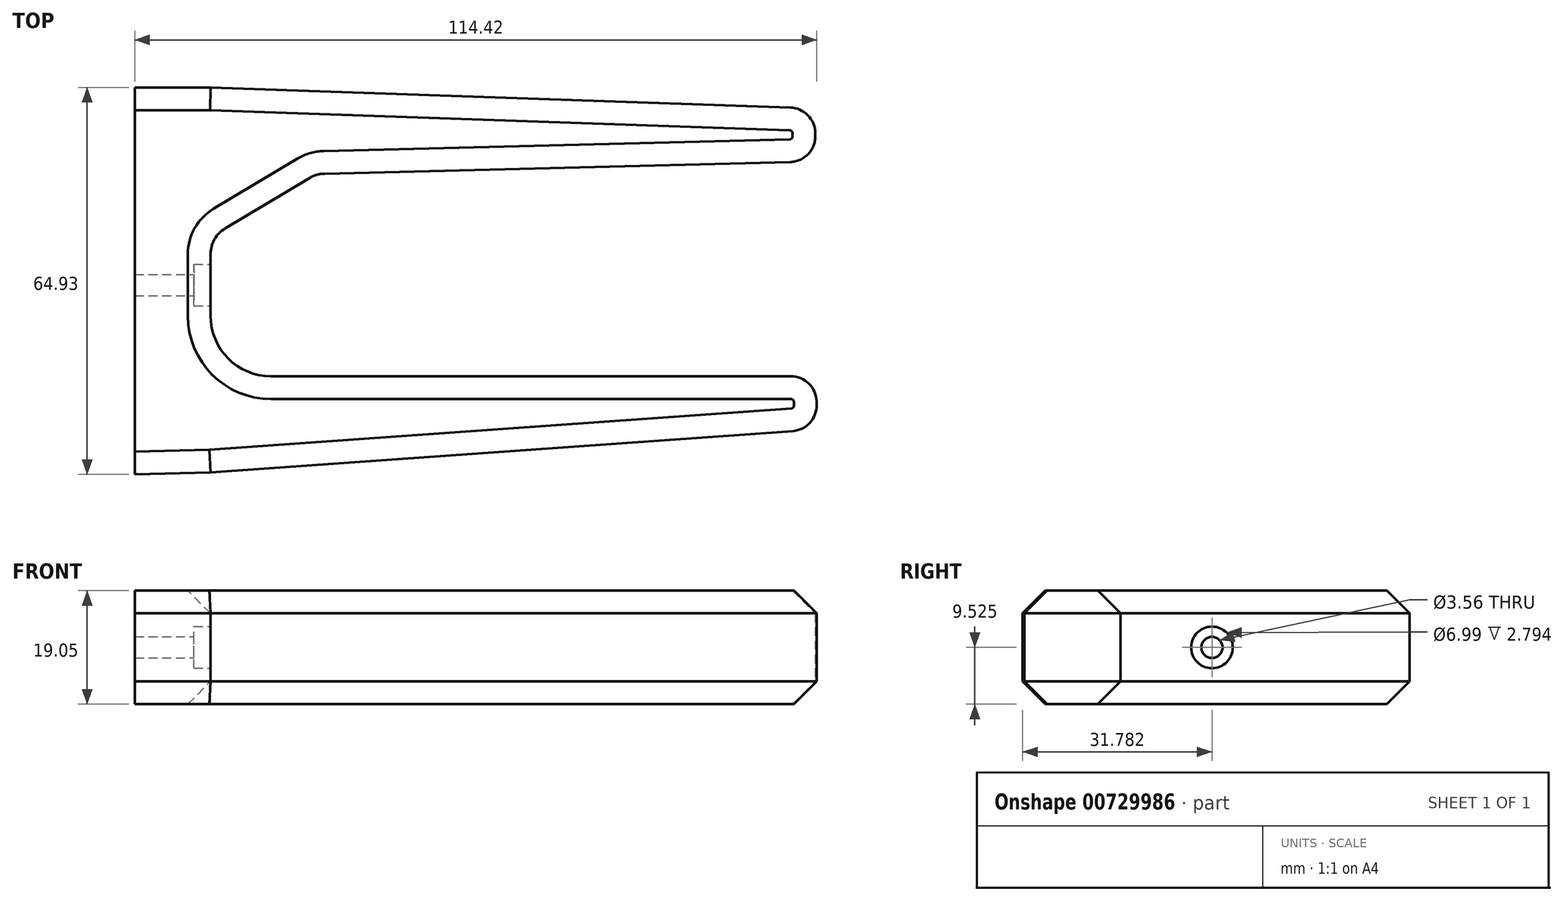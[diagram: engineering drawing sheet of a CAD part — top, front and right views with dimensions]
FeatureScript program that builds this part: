
annotation { "Feature Type Name" : "Feature", "Feature Type Description" : "" }
export const myFeature = defineFeature(function(context is Context, id is Id, definition is map)
    precondition{}
    {
        {
            var Q0;
            Q0=qCreatedBy(makeId("Top.planeOp"),FACE);
            var sketch = newSketch(context, id + "F0", { "sketchPlane" : qUnion([Q0])});
            skLineSegment(sketch, "E0", {"start": v(0, 0) * mm, "end": v(101.6, 0) * mm});
            skLineSegment(sketch, "E1", {"start": v(0, 0) * mm, "end": v(0, 33.53) * mm});
            skLineSegment(sketch, "E2", {"start": v(101.6, 0) * mm, "end": v(101.6, 36.07) * mm});
            skLineSegment(sketch, "E3", {"start": v(0, 33.53) * mm, "end": v(101.6, 36.07) * mm});
            skLineSegment(sketch, "E4", {"start": v(101.6, 36.07) * mm, "end": v(101.38, 44.96) * mm});
            skLineSegment(sketch, "E5", {"start": v(101.38, 44.96) * mm, "end": v(0, 48.47) * mm});
            skLineSegment(sketch, "E6", {"start": v(0, 48.47) * mm, "end": v(-12.7, 48.47) * mm});
            skLineSegment(sketch, "E7", {"start": v(-12.7, 48.47) * mm, "end": v(-12.7, 0) * mm});
            skLineSegment(sketch, "E8", {"start": v(101.6, 0) * mm, "end": v(101.82, -8.89) * mm});
            skLineSegment(sketch, "E9", {"start": v(101.82, -8.89) * mm, "end": v(0, -16.15) * mm});
            skLineSegment(sketch, "E10", {"start": v(0, -16.15) * mm, "end": v(-12.7, -16.46) * mm});
            skLineSegment(sketch, "E11", {"start": v(-12.7, -16.46) * mm, "end": v(-12.7, 0) * mm});
            skSolve(sketch);
        }
        {
            var Q0;
            Q0=makeQuery(id+"F0.imprint","IMPRINT",FACE,{"disambiguationData":[TD([[makeQuery(id+"F0.imprint","IMPRINT",EDGE,{"derivedFrom":sQuery(id+"F0.wireOp",EDGE,"E0")}),-1.0]])]});
            extrude(context, id + "F1", {"entities" : qUnion([Q0]), "depth" : 19.05 * mm, "offsetDistance" : 25.4 * mm});
        }
        {
            var Q0;
            Q0=makeQuery(id+"F1.opExtrude","SWEPT_EDGE",EDGE,{"disambiguationData":[OSD([sQuery(id+"F0.wireOp",EDGE,"E1"),sQuery(id+"F0.wireOp",EDGE,"E3")])]});
            chamfer(context, id + "F2", {"entities" : qUnion([Q0]), "chamferType" : ChamferType.TWO_OFFSETS, "width1" : 10.16 * mm, "oppositeDirection" : true, "width2" : 17.78 * mm, "tangentPropagation" : true});
        }
        {
            var Q0;
            {var subQ0=sQuery(id+"F0.wireOp",EDGE,"E3");Q0=makeQuery(id+"F2.opChamfer","BLEND_EDGE",EDGE,{"blendedFrom":[makeQuery(id+"F1.opExtrude","SWEPT_EDGE",EDGE,{"disambiguationData":[OSD([sQuery(id+"F0.wireOp",EDGE,"E1"),subQ0])]}),makeQuery(id+"F1.opExtrude","SWEPT_FACE",FACE,{"disambiguationData":[OSD([subQ0])]})],"blendedInto":[makeQuery(id+"F1.opExtrude","SWEPT_FACE",FACE,{"disambiguationData":[OSD([subQ0])]})]});}
            var Q1;
            {var subQ0=sQuery(id+"F0.wireOp",EDGE,"E1");Q1=makeQuery(id+"F2.opChamfer","BLEND_EDGE",EDGE,{"blendedFrom":[makeQuery(id+"F1.opExtrude","SWEPT_EDGE",EDGE,{"disambiguationData":[OSD([subQ0,sQuery(id+"F0.wireOp",EDGE,"E3")])]}),makeQuery(id+"F1.opExtrude","SWEPT_FACE",FACE,{"disambiguationData":[OSD([subQ0])]})],"blendedInto":[makeQuery(id+"F1.opExtrude","SWEPT_FACE",FACE,{"disambiguationData":[OSD([subQ0])]})]});}
            fillet(context, id + "F3", {"entities" : qUnion([Q0, Q1]), "radius" : 5.08 * mm, "tangentPropagation" : true, "allowEdgeOverflow" : false});
        }
        {
            var Q0;
            Q0=makeQuery(id+"F1.opExtrude","SWEPT_EDGE",EDGE,{"disambiguationData":[OSD([sQuery(id+"F0.wireOp",EDGE,"E0"),sQuery(id+"F0.wireOp",EDGE,"E1")])]});
            fillet(context, id + "F4", {"entities" : qUnion([Q0]), "radius" : 10.16 * mm, "tangentPropagation" : true, "allowEdgeOverflow" : false});
        }
        {
            var Q0;
            Q0=makeQuery(id+"F1.opExtrude","SWEPT_EDGE",EDGE,{"disambiguationData":[OSD([sQuery(id+"F0.wireOp",EDGE,"E2"),sQuery(id+"F0.wireOp",EDGE,"E3"),sQuery(id+"F0.wireOp",EDGE,"E4")])]});
            var Q1;
            Q1=makeQuery(id+"F1.opExtrude","SWEPT_EDGE",EDGE,{"disambiguationData":[OSD([sQuery(id+"F0.wireOp",EDGE,"E4"),sQuery(id+"F0.wireOp",EDGE,"E5")])]});
            var Q2;
            Q2=makeQuery(id+"F1.opExtrude","SWEPT_EDGE",EDGE,{"disambiguationData":[OSD([sQuery(id+"F0.wireOp",EDGE,"E0"),sQuery(id+"F0.wireOp",EDGE,"E2"),sQuery(id+"F0.wireOp",EDGE,"E8")])]});
            var Q3;
            Q3=makeQuery(id+"F1.opExtrude","SWEPT_EDGE",EDGE,{"disambiguationData":[OSD([sQuery(id+"F0.wireOp",EDGE,"E8"),sQuery(id+"F0.wireOp",EDGE,"E9")])]});
            fillet(context, id + "F5", {"entities" : qUnion([Q0, Q1, Q2, Q3]), "radius" : 4.32 * mm, "tangentPropagation" : true, "allowEdgeOverflow" : false});
        }
        {
            var Q0;
            Q0=makeQuery(id+"F1.opExtrude","CAP_EDGE",EDGE,{"disambiguationData":[OSD([sQuery(id+"F0.wireOp",EDGE,"E6")])],"isStart":false});
            var Q1;
            Q1=makeQuery(id+"F1.opExtrude","CAP_EDGE",EDGE,{"disambiguationData":[OSD([sQuery(id+"F0.wireOp",EDGE,"E10")])],"isStart":false});
            var Q2;
            Q2=makeQuery(id+"F1.opExtrude","CAP_EDGE",EDGE,{"disambiguationData":[OSD([sQuery(id+"F0.wireOp",EDGE,"E6")])],"isStart":true});
            var Q3;
            Q3=makeQuery(id+"F1.opExtrude","CAP_EDGE",EDGE,{"disambiguationData":[OSD([sQuery(id+"F0.wireOp",EDGE,"E10")])],"isStart":true});
            var Q4;
            Q4=makeQuery(id+"F1.opExtrude","CAP_EDGE",EDGE,{"disambiguationData":[OSD([sQuery(id+"F0.wireOp",EDGE,"E3")])],"isStart":false});
            var Q5;
            Q5=makeQuery(id+"F1.opExtrude","CAP_EDGE",EDGE,{"disambiguationData":[OSD([sQuery(id+"F0.wireOp",EDGE,"E3")])],"isStart":true});
            chamfer(context, id + "F6", {"entities" : qUnion([Q0, Q1, Q2, Q3, Q4, Q5]), "width" : 3.8 * mm, "tangentPropagation" : true});
        }
        {
            var Q0;
            Q0=makeQuery(id+"F1.opExtrude","SWEPT_FACE",FACE,{"disambiguationData":[OSD([sQuery(id+"F0.wireOp",EDGE,"E1")])]});
            var sketch = newSketch(context, id + "F7", { "sketchPlane" : qUnion([Q0])});
            skCircle(sketch, "E12", {"center": v(15.32, 9.53) * mm, "radius": 1.78 * mm});
            skPoint(sketch, "E12.centerSnap0", {"position": v(15.32, 15.24) * mm});
            skPoint(sketch, "E12.centerSnap1", {"position": v(20.48, 9.53) * mm});
            skCircle(sketch, "E13", {"center": v(15.32, 9.53) * mm, "radius": 3.5 * mm});
            skSolve(sketch);
        }
        {
            var Q0;
            Q0=makeQuery(id+"F7.imprint","IMPRINT",FACE,{"disambiguationData":[TD([[makeQuery(id+"F7.imprint","IMPRINT",EDGE,{"derivedFrom":sQuery(id+"F7.wireOp",EDGE,"E12")}),1.0]])]});
            extrude(context, id + "F8", {"entities" : qUnion([Q0]), "operationType" : NewBodyOperationType.REMOVE, "endBound" : BoundingType.THROUGH_ALL, "oppositeDirection" : true, "depth" : 25.4 * mm, "offsetDistance" : 25.4 * mm});
        }
        {
            var Q0;
            Q0=makeQuery(id+"F7.imprint","IMPRINT",FACE,{"disambiguationData":[TD([[makeQuery(id+"F7.imprint","IMPRINT",EDGE,{"derivedFrom":sQuery(id+"F7.wireOp",EDGE,"E12")}),-1.0]])]});
            extrude(context, id + "F9", {"entities" : qUnion([Q0]), "operationType" : NewBodyOperationType.REMOVE, "oppositeDirection" : true, "depth" : 2.8 * mm, "offsetDistance" : 25.4 * mm});
        }
    });
